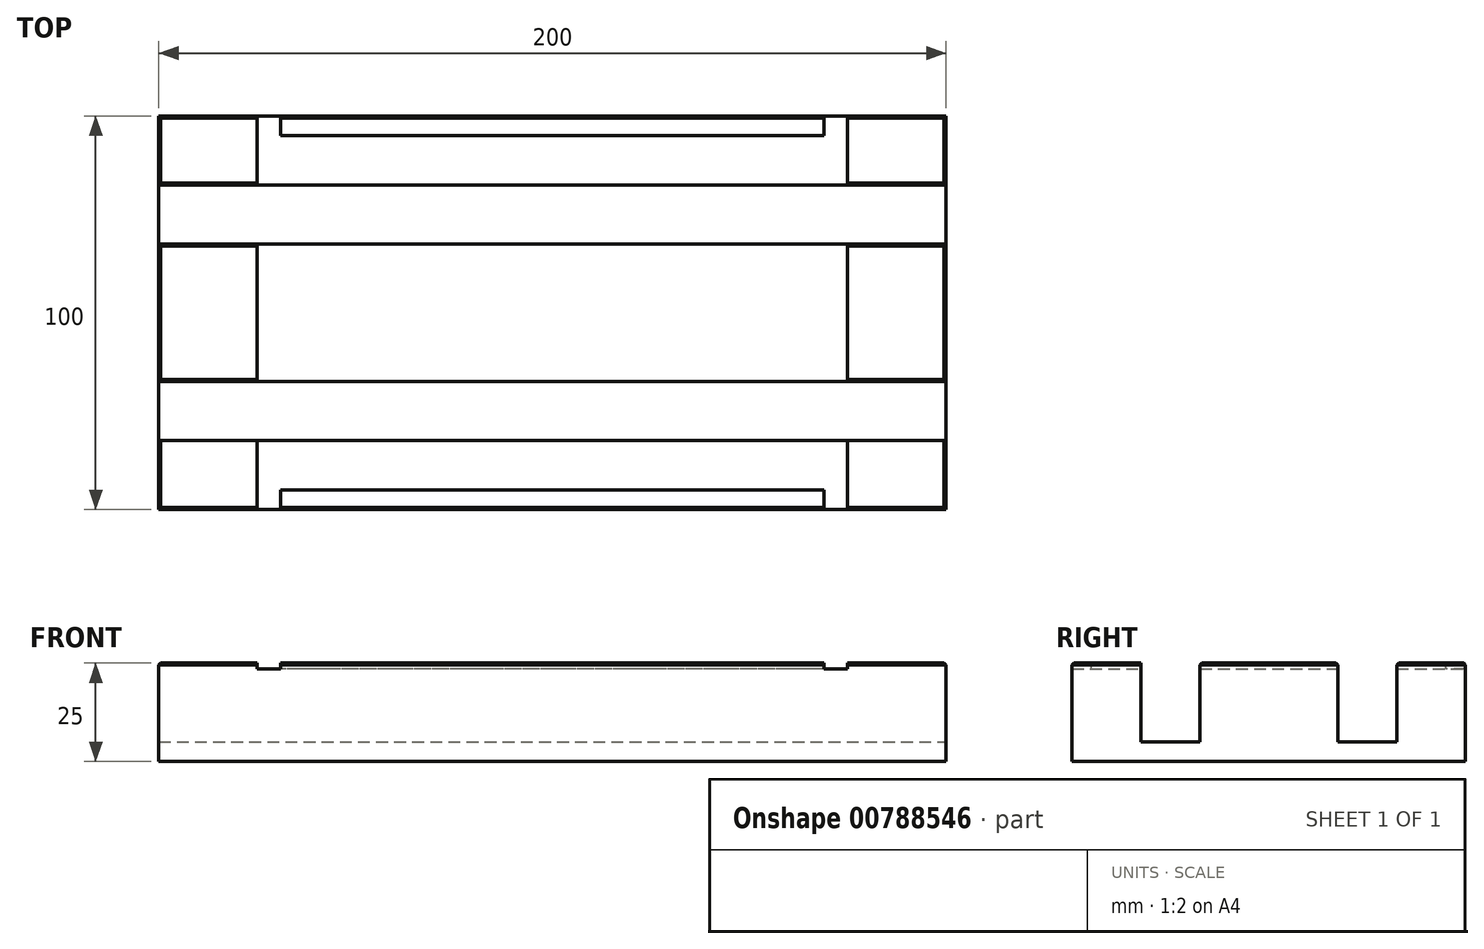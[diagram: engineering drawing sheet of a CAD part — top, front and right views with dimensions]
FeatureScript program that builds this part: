
annotation { "Feature Type Name" : "Feature", "Feature Type Description" : "" }
export const myFeature = defineFeature(function(context is Context, id is Id, definition is map)
    precondition{}
    {
        {
            var Q0;
            Q0=qCreatedBy(makeId("Top.planeOp"),FACE);
            var sketch = newSketch(context, id + "F0", { "sketchPlane" : qUnion([Q0])});
            skLineSegment(sketch, "E0.bottom", {"start": v(-100, 50) * mm, "end": v(100, 50) * mm});
            skLineSegment(sketch, "E0.top", {"start": v(-100, -50) * mm, "end": v(100, -50) * mm});
            skLineSegment(sketch, "E0.left", {"start": v(-100, 50) * mm, "end": v(-100, -50) * mm});
            skLineSegment(sketch, "E0.right", {"start": v(100, 50) * mm, "end": v(100, -50) * mm});
            skPoint(sketch, "E0.middle", {"position": v(0, 0) * mm});
            skSolve(sketch);
        }
        {
            var Q0;
            Q0 = qSketchRegion(id + "F0", true);
            extrude(context, id + "F1", {"entities" : qUnion([Q0]), "oppositeDirection" : true, "depth" : 25 * mm, "offsetDistance" : 25 * mm});
        }
        {
            var Q0;
            Q0=makeQuery(id+"F1.opExtrude","CAP_FACE",FACE,{"disambiguationData":[OSD([sQuery(id+"F0.wireOp",EDGE,"E0.bottom"),sQuery(id+"F0.wireOp",EDGE,"E0.top"),sQuery(id+"F0.wireOp",EDGE,"E0.left"),sQuery(id+"F0.wireOp",EDGE,"E0.right")])],"isStart":true});
            var sketch = newSketch(context, id + "F2", { "sketchPlane" : qUnion([Q0])});
            skLineSegment(sketch, "E1", {"start": v(-100, 0) * mm, "end": v(100, 0) * mm, "construction": true});
            skLineSegment(sketch, "E2", {"start": v(0, 50) * mm, "end": v(0, -50) * mm, "construction": true});
            skLineSegment(sketch, "E3.0", {"start": v(-100, -25) * mm, "end": v(100, -25) * mm, "construction": true});
            skLineSegment(sketch, "E4.MirrorCS", {"start": v(-100, 25) * mm, "end": v(100, 25) * mm, "construction": true});
            skLineSegment(sketch, "E5.0", {"start": v(-100, -32.5) * mm, "end": v(100, -32.5) * mm});
            skLineSegment(sketch, "E6.MirrorCS", {"start": v(-100, -17.5) * mm, "end": v(100, -17.5) * mm});
            skLineSegment(sketch, "E7.0", {"start": v(-100, 17.5) * mm, "end": v(100, 17.5) * mm});
            skLineSegment(sketch, "E8.MirrorCS", {"start": v(-100, 32.5) * mm, "end": v(100, 32.5) * mm});
            skLineSegment(sketch, "E9", {"start": v(-100, 32.5) * mm, "end": v(-100, 17.5) * mm});
            skLineSegment(sketch, "E10", {"start": v(100, 32.5) * mm, "end": v(100, 17.5) * mm});
            skLineSegment(sketch, "E11", {"start": v(100, -17.5) * mm, "end": v(100, -32.5) * mm});
            skLineSegment(sketch, "E12", {"start": v(-100, -17.5) * mm, "end": v(-100, -32.5) * mm});
            skSolve(sketch);
        }
        {
            var Q0;
            Q0=makeQuery(id+"F2.imprint","IMPRINT",FACE,{"disambiguationData":[TD([[makeQuery(id+"F2.imprint","IMPRINT",EDGE,{"derivedFrom":sQuery(id+"F2.wireOp",EDGE,"E7.0")}),1.0]])]});
            var Q1;
            Q1=makeQuery(id+"F2.imprint","IMPRINT",FACE,{"disambiguationData":[TD([[makeQuery(id+"F2.imprint","IMPRINT",EDGE,{"derivedFrom":sQuery(id+"F2.wireOp",EDGE,"E5.0")}),1.0]])]});
            extrude(context, id + "F3", {"entities" : qUnion([Q0, Q1]), "operationType" : NewBodyOperationType.REMOVE, "oppositeDirection" : true, "depth" : 20 * mm, "offsetDistance" : 25 * mm});
        }
        {
            var Q0;
            Q0=makeQuery(id+"F1.opExtrude","CAP_EDGE",EDGE,{"disambiguationData":[OSD([sQuery(id+"F0.wireOp",EDGE,"E0.top")])],"isStart":true});
            var Q1;
            Q1=makeQuery(id+"F3.boolean.opBoolean","COPY",EDGE,{"derivedFrom":makeQuery(id+"F3.opExtrude","CAP_EDGE",EDGE,{"disambiguationData":[OSD([sQuery(id+"F2.wireOp",EDGE,"E5.0")])],"isStart":true})});
            var Q2;
            Q2=makeQuery(id+"F3.boolean.opBoolean","COPY",EDGE,{"derivedFrom":makeQuery(id+"F3.opExtrude","CAP_EDGE",EDGE,{"disambiguationData":[OSD([sQuery(id+"F2.wireOp",EDGE,"E6.MirrorCS")])],"isStart":true})});
            var Q3;
            Q3=makeQuery(id+"F3.boolean.opBoolean","COPY",EDGE,{"derivedFrom":makeQuery(id+"F3.opExtrude","CAP_EDGE",EDGE,{"disambiguationData":[OSD([sQuery(id+"F2.wireOp",EDGE,"E7.0")])],"isStart":true})});
            var Q4;
            Q4=makeQuery(id+"F3.boolean.opBoolean","COPY",EDGE,{"derivedFrom":makeQuery(id+"F3.opExtrude","CAP_EDGE",EDGE,{"disambiguationData":[OSD([sQuery(id+"F2.wireOp",EDGE,"E8.MirrorCS")])],"isStart":true})});
            var Q5;
            Q5=makeQuery(id+"F1.opExtrude","CAP_EDGE",EDGE,{"disambiguationData":[OSD([sQuery(id+"F0.wireOp",EDGE,"E0.bottom")])],"isStart":true});
            var Q6;
            {var subQ0=sQuery(id+"F0.wireOp",EDGE,"E0.right");var subQ1=sQuery(id+"F0.wireOp",EDGE,"E0.top");Q6=makeQuery(id+"F3.boolean.opBoolean","SPLIT",EDGE,{"disambiguationData":[TD([makeQuery(id+"F1.opExtrude","SWEPT_FACE",FACE,{"disambiguationData":[OSD([subQ1])]})])],"derivedFrom":makeQuery(id+"F1.opExtrude","CAP_EDGE",EDGE,{"disambiguationData":[OSD([subQ0])],"isStart":true})});}
            var Q7;
            {var subQ0=sQuery(id+"F0.wireOp",EDGE,"E0.right");Q7=makeQuery(id+"F3.boolean.opBoolean","SPLIT",EDGE,{"disambiguationData":[TD([makeQuery(id+"F3.opExtrude","SWEPT_FACE",FACE,{"disambiguationData":[OSD([sQuery(id+"F2.wireOp",EDGE,"E6.MirrorCS")])]})])],"derivedFrom":makeQuery(id+"F1.opExtrude","CAP_EDGE",EDGE,{"disambiguationData":[OSD([subQ0])],"isStart":true})});}
            var Q8;
            {var subQ0=sQuery(id+"F0.wireOp",EDGE,"E0.bottom");var subQ1=sQuery(id+"F0.wireOp",EDGE,"E0.right");Q8=makeQuery(id+"F3.boolean.opBoolean","SPLIT",EDGE,{"disambiguationData":[TD([makeQuery(id+"F1.opExtrude","SWEPT_FACE",FACE,{"disambiguationData":[OSD([subQ0])]})])],"derivedFrom":makeQuery(id+"F1.opExtrude","CAP_EDGE",EDGE,{"disambiguationData":[OSD([subQ1])],"isStart":true})});}
            var Q9;
            {var subQ0=sQuery(id+"F0.wireOp",EDGE,"E0.bottom");var subQ1=sQuery(id+"F0.wireOp",EDGE,"E0.left");Q9=makeQuery(id+"F3.boolean.opBoolean","SPLIT",EDGE,{"disambiguationData":[TD([makeQuery(id+"F1.opExtrude","SWEPT_FACE",FACE,{"disambiguationData":[OSD([subQ0])]})])],"derivedFrom":makeQuery(id+"F1.opExtrude","CAP_EDGE",EDGE,{"disambiguationData":[OSD([subQ1])],"isStart":true})});}
            var Q10;
            {var subQ0=sQuery(id+"F0.wireOp",EDGE,"E0.left");Q10=makeQuery(id+"F3.boolean.opBoolean","SPLIT",EDGE,{"disambiguationData":[TD([makeQuery(id+"F3.opExtrude","SWEPT_FACE",FACE,{"disambiguationData":[OSD([sQuery(id+"F2.wireOp",EDGE,"E6.MirrorCS")])]})])],"derivedFrom":makeQuery(id+"F1.opExtrude","CAP_EDGE",EDGE,{"disambiguationData":[OSD([subQ0])],"isStart":true})});}
            var Q11;
            {var subQ0=sQuery(id+"F0.wireOp",EDGE,"E0.left");var subQ1=sQuery(id+"F0.wireOp",EDGE,"E0.top");Q11=makeQuery(id+"F3.boolean.opBoolean","SPLIT",EDGE,{"disambiguationData":[TD([makeQuery(id+"F1.opExtrude","SWEPT_FACE",FACE,{"disambiguationData":[OSD([subQ1])]})])],"derivedFrom":makeQuery(id+"F1.opExtrude","CAP_EDGE",EDGE,{"disambiguationData":[OSD([subQ0])],"isStart":true})});}
            chamfer(context, id + "F4", {"entities" : qUnion([Q0, Q1, Q2, Q3, Q4, Q5, Q6, Q7, Q8, Q9, Q10, Q11]), "width" : 0.5 * mm, "tangentPropagation" : true});
        }
        {
            var Q0;
            Q0=qCreatedBy(makeId("Top.planeOp"),FACE);
            var sketch = newSketch(context, id + "F5", { "sketchPlane" : qUnion([Q0])});
            skLineSegment(sketch, "E13.bottom", {"start": v(69, 45) * mm, "end": v(-69, 45) * mm});
            skLineSegment(sketch, "E13.top", {"start": v(69, -45) * mm, "end": v(-69, -45) * mm});
            skPoint(sketch, "E13.middle", {"position": v(0, 0) * mm});
            skArc(sketch, "E14", {"start": v(-69, 55) * mm, "mid": v(-72, 58) * mm, "end": v(-75, 55) * mm});
            skCircle(sketch, "E15", {"center": v(-72, -55) * mm, "radius": 3 * mm});
            skLineSegment(sketch, "E16", {"start": v(-69, 55) * mm, "end": v(-69, 45) * mm});
            skLineSegment(sketch, "E17", {"start": v(-75, 55) * mm, "end": v(-75, 55) * mm});
            skLineSegment(sketch, "E18", {"start": v(-105.98, 0) * mm, "end": v(109.32, 0) * mm, "construction": true});
            skLineSegment(sketch, "E19", {"start": v(0, 53.8) * mm, "end": v(0, -51.55) * mm, "construction": true});
            skLineSegment(sketch, "E20.MirrorCS", {"start": v(69, 55) * mm, "end": v(69, 45) * mm});
            skArc(sketch, "E21.MirrorCS", {"start": v(69, 55) * mm, "mid": v(72, 58) * mm, "end": v(75, 55) * mm});
            skLineSegment(sketch, "E22.MirrorCS", {"start": v(75, 55) * mm, "end": v(75, 0) * mm});
            skLineSegment(sketch, "E23.MirrorCS", {"start": v(-69, -55) * mm, "end": v(-69, -45) * mm});
            skArc(sketch, "E24.MirrorCS", {"start": v(-69, -55) * mm, "mid": v(-72, -58) * mm, "end": v(-75, -55) * mm});
            skLineSegment(sketch, "E25.MirrorCS", {"start": v(69, -55) * mm, "end": v(69, -45) * mm});
            skArc(sketch, "E26.MirrorCS", {"start": v(69, -55) * mm, "mid": v(72, -58) * mm, "end": v(75, -55) * mm});
            skLineSegment(sketch, "E27.MirrorCS", {"start": v(75, -55) * mm, "end": v(75, 0) * mm});
            skLineSegment(sketch, "E28", {"start": v(-75, -55) * mm, "end": v(-75, 55) * mm});
            skSolve(sketch);
        }
        {
            var Q0;
            Q0=makeQuery(id+"F5.imprint","IMPRINT",FACE,{"disambiguationData":[TD([[makeQuery(id+"F5.imprint","IMPRINT",EDGE,{"derivedFrom":sQuery(id+"F5.wireOp",EDGE,"E13.bottom")}),1.0]])]});
            extrude(context, id + "F6", {"entities" : qUnion([Q0]), "operationType" : NewBodyOperationType.REMOVE, "oppositeDirection" : true, "depth" : 1.5 * mm, "offsetDistance" : 25 * mm});
        }
    });
